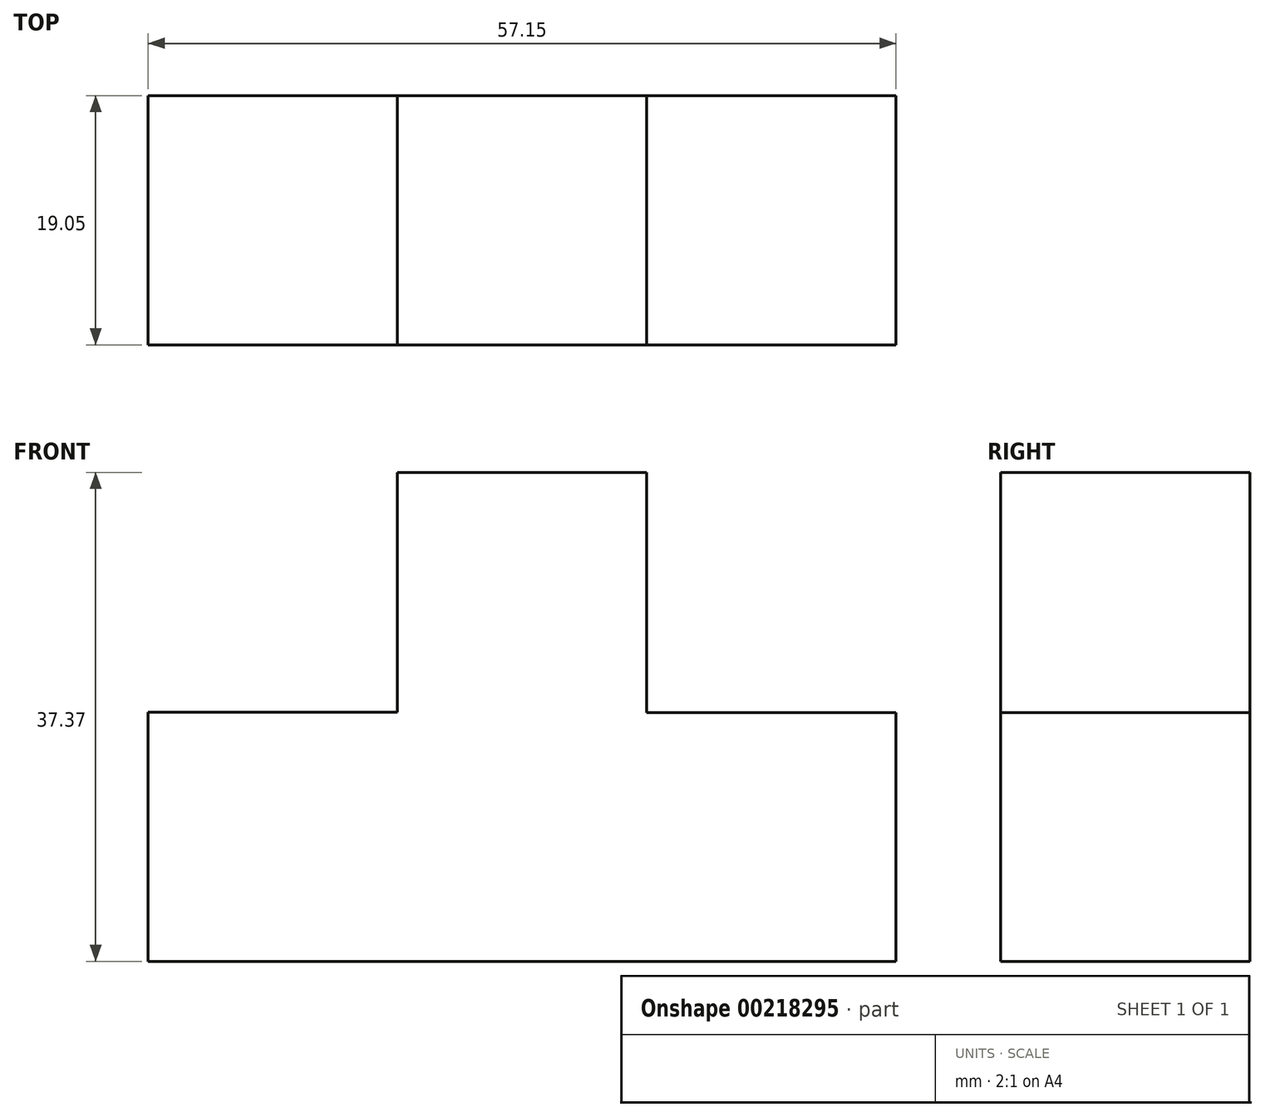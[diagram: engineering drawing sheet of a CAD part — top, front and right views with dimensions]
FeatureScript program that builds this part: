
annotation { "Feature Type Name" : "Feature", "Feature Type Description" : "" }
export const myFeature = defineFeature(function(context is Context, id is Id, definition is map)
    precondition{}
    {
        {
            var Q0;
            Q0=qCreatedBy(makeId("Front.planeOp"),FACE);
            var sketch = newSketch(context, id + "F0", { "sketchPlane" : qUnion([Q0])});
            skLineSegment(sketch, "E0", {"start": v(-38.1, 0) * mm, "end": v(19.05, 0) * mm});
            skLineSegment(sketch, "E1", {"start": v(19.05, 0) * mm, "end": v(19.05, 19.02) * mm});
            skLineSegment(sketch, "E2", {"start": v(-38.1, 19.05) * mm, "end": v(-38.1, 0) * mm});
            skLineSegment(sketch, "E3", {"start": v(-38.1, 19.05) * mm, "end": v(-19.05, 19.05) * mm});
            skLineSegment(sketch, "E4", {"start": v(19.05, 19.02) * mm, "end": v(0, 19.02) * mm});
            skLineSegment(sketch, "E5", {"start": v(-19.05, 19.05) * mm, "end": v(-19.05, 37.37) * mm});
            skLineSegment(sketch, "E6", {"start": v(-19.05, 37.37) * mm, "end": v(0, 37.37) * mm});
            skLineSegment(sketch, "E7", {"start": v(0, 37.37) * mm, "end": v(0, 19.02) * mm});
            skSolve(sketch);
        }
        {
            var Q0;
            Q0=makeQuery(id+"F0.imprint","IMPRINT",FACE,{"disambiguationData":[TD([[makeQuery(id+"F0.imprint","IMPRINT",EDGE,{"derivedFrom":sQuery(id+"F0.wireOp",EDGE,"E0")}),1.0]])]});
            extrude(context, id + "F1", {"entities" : qUnion([Q0]), "depth" : 19.05 * mm});
        }
    });
